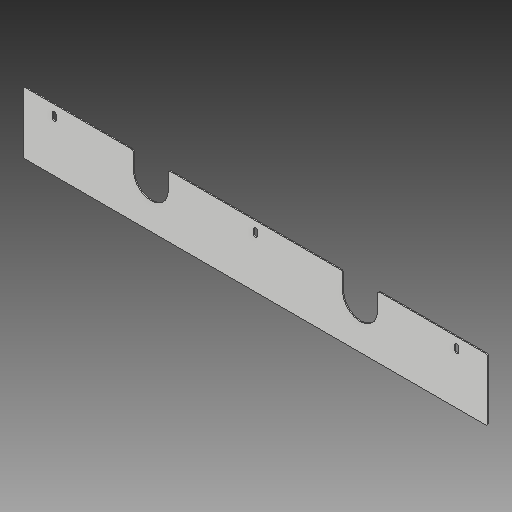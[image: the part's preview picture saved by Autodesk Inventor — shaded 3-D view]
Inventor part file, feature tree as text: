
AUTODESK INVENTOR PART (.ipt)
format: ipt  version: 2019 (Build 230136000, 136)  size: 172,544 bytes
history: native  units: mm
features: reference x8, other x4, extrude x2, fillet x2, sketch x2, helix x1
ambient origin geometry x8: Origin, YZ Plane, XZ Plane, XY Plane, X Axis, Y Axis, Z Axis, Center Point
bodies: Body1 (feature_tree)
feature tree (19):
  extrude  "Extrusion2"  Depth=4.0mm
  fillet  "Fillet2"  Radius=4.0mm
  extrude  "Extrusion3"  Depth=4.0mm
  fillet  "Fillet3"  Radius=1.0mm
  sketch  "Sketch1"  dims[d0=2.0mm d1=58.0mm d5=4.0mm]
  reference  "Reference2"
  sketch  "Sketch2"  dims[d6=4.0mm d7=4.0mm d8=1.0mm d9=0.0mm d10=2.0mm d13=17.0mm d14=1.0mm d15=0.0mm d16=2.0mm d17=10.0mm d18=10.0mm]
  reference  "Reference3"
  reference  "Reference4"
  reference  "Reference5"
  reference  "Reference6"
  reference  "Reference7"
  reference  "Reference8"
  reference  "Reference9"
  other  "<userpath>\Documents\CAD Files\Helix DLP\Helix DLP.iam"
  helix  "Helix DLP.iam"  [1 undecoded]
  other  "Tank2:1"
  other  "wiper:1"
  other  "Wiper_Arm_1:1"
note: 1 required parameter value undecoded (feature->parameter linkage not recoverable at this tier; creation-order binding heuristic only, values carry confidence <= 0.55)
